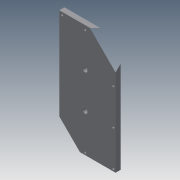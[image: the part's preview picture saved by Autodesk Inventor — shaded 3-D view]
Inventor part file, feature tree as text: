
AUTODESK INVENTOR PART (.ipt)
format: ipt  version: 2015 (Build 190159000, 159)  size: 119,296 bytes
history: native  units: mm
features: extrude x1, sketch x1
ambient origin geometry x8: Origin, YZ Plane, XZ Plane, XY Plane, X Axis, Y Axis, Z Axis, Center Point
bodies: Body1 (feature_tree)
feature tree (2):
  extrude  "Extrusion5"  Depth=10.0mm
  sketch  "Sketch1"  dims[d2=200.0mm d5=10.0mm d9=70.0mm d13=35.0mm d14=50.0mm d17=75.0mm d18=185.0mm d19=35.0mm d22=5.0mm d23=5.0mm d24=5.0mm d25=5.0mm d26=5.0mm d27=5.0mm d28=5.0mm d29=5.0mm d30=5.0mm d31=5.0mm d32=5.0mm d33=75.0mm d34=5.0mm d35=75.0mm d36=5.0mm d37=5.0mm d38=5.0mm d39=5.0mm d42=5.0mm d43=50.0mm d46=5.0mm d47=5.0mm d48=50.0mm d49=10.0mm d50=0.0mm]
